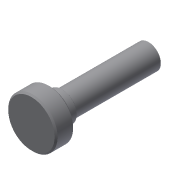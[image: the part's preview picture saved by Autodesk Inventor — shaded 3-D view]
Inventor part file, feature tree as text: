
AUTODESK INVENTOR PART (.ipt)
format: ipt  version: 2017 (Build 210142000, 142)  size: 120,320 bytes
history: native  units: in
note: dims shown in document units (in); Inventor stores cm internally (conversion verified against a paired STEP export)
features: revolve x1, chamfer x1, fillet x1, sketch x1
ambient origin geometry x8: Origin, YZ Plane, XZ Plane, XY Plane, X Axis, Y Axis, Z Axis, Center Point
bodies: Solid1 (feature_tree)
feature tree (4):
  revolve  "Revolution1"  [1 undecoded]
  chamfer  "Chamfer1"  Distance=0.5in
  fillet  "Fillet1"  Radius=0.6in
  sketch  "Sketch1"  dims[d0=0.75in d1=1.0in d2=0.5in d3=0.6in d4=4.75in d5=3.5in d6=90.0deg d7=0.06in d8=0.125in d9=45.0deg d10=0.02in]
note: 1 required parameter value undecoded (feature->parameter linkage not recoverable at this tier; creation-order binding heuristic only, values carry confidence <= 0.55)
